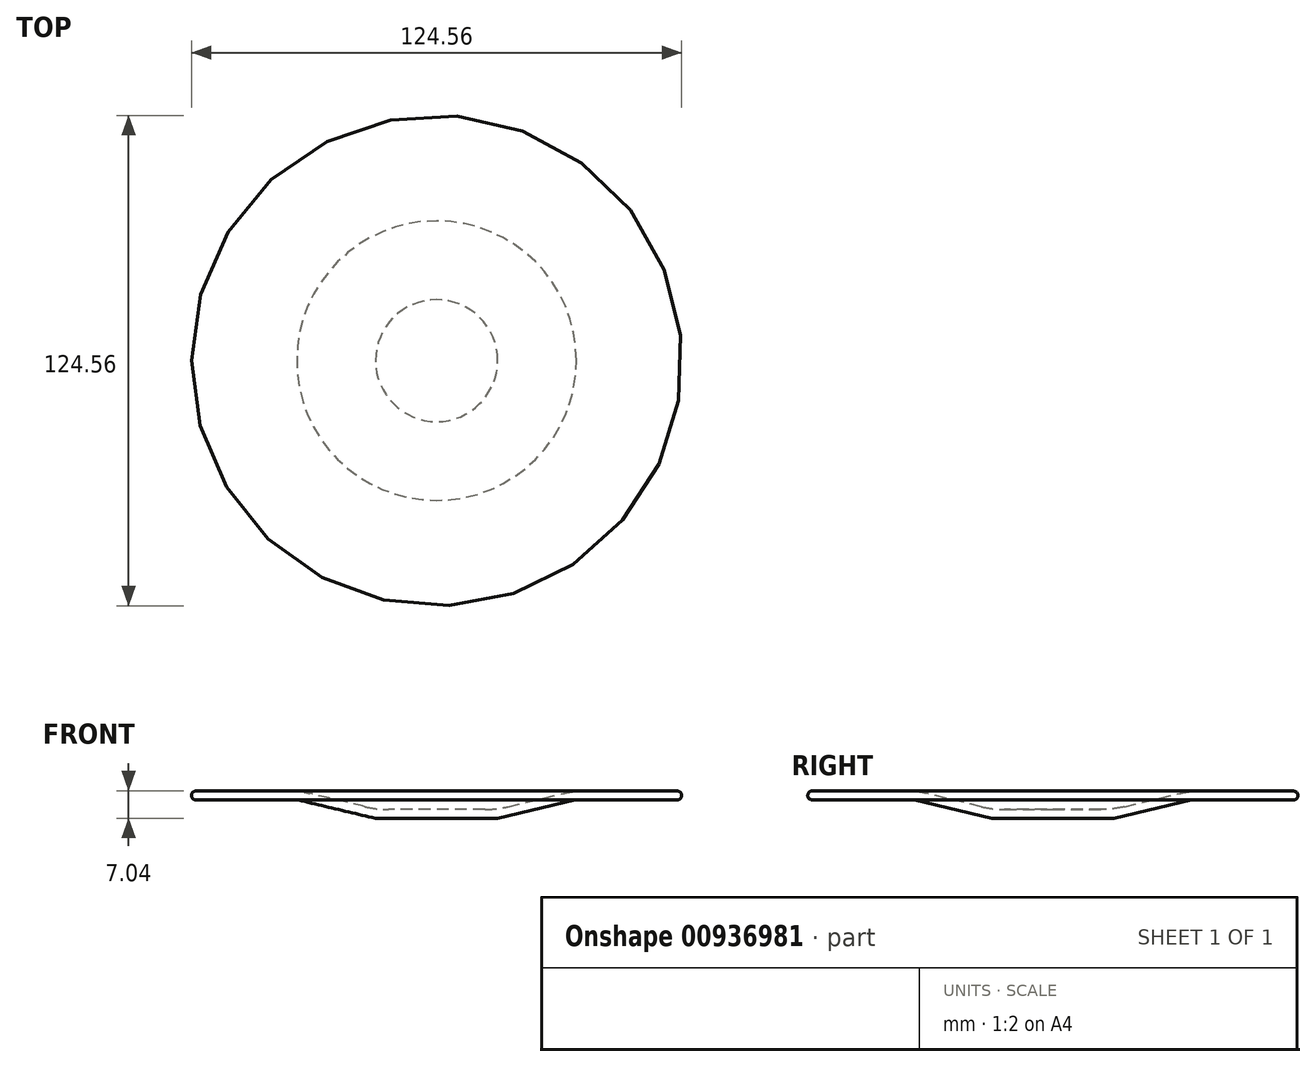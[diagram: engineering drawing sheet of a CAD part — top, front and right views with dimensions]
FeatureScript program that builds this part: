
annotation { "Feature Type Name" : "Feature", "Feature Type Description" : "" }
export const myFeature = defineFeature(function(context is Context, id is Id, definition is map)
    precondition{}
    {
        {
            var Q0;
            Q0=qCreatedBy(makeId("Front.planeOp"),FACE);
            var sketch = newSketch(context, id + "F0", { "sketchPlane" : qUnion([Q0])});
            skLineSegment(sketch, "E0", {"start": v(15.24, 0) * mm, "end": v(0, 0) * mm});
            skLineSegment(sketch, "E1", {"start": v(15.24, 0) * mm, "end": v(35.24, 4.76) * mm});
            skLineSegment(sketch, "E2", {"start": v(35.24, 4.76) * mm, "end": v(61.14, 4.68) * mm});
            skLineSegment(sketch, "E3", {"start": v(0, 0) * mm, "end": v(0, -2.29) * mm});
            skLineSegment(sketch, "E4.0", {"start": v(15.5, -2.29) * mm, "end": v(0, -2.29) * mm});
            skLineSegment(sketch, "E4.1", {"start": v(15.5, -2.29) * mm, "end": v(35.5, 2.47) * mm});
            skLineSegment(sketch, "E4.2", {"start": v(35.5, 2.47) * mm, "end": v(61.14, 2.39) * mm});
            skArc(sketch, "E5", {"start": v(61.14, 2.39) * mm, "mid": v(62.28, 3.53) * mm, "end": v(61.14, 4.68) * mm});
            skSolve(sketch);
        }
        {
            var Q0;
            Q0=qCreatedBy(makeId("Front.planeOp"),FACE);
            var sketch = newSketch(context, id + "F1", { "sketchPlane" : qUnion([Q0])});
            skLineSegment(sketch, "E6", {"start": v(0, -16.07) * mm, "end": v(0, 24.38) * mm, "construction": true});
            skSolve(sketch);
        }
        {
            var Q0;
            Q0=makeQuery(id+"F0.imprint","IMPRINT",FACE,{"disambiguationData":[TD([[makeQuery(id+"F0.imprint","IMPRINT",EDGE,{"derivedFrom":sQuery(id+"F0.wireOp",EDGE,"E0")}),1.0]])]});
            var Q1;
            Q1=sQuery(id+"F1.wireOp",EDGE,"E6");
            revolve(context, id + "F2", {"surfaceOperationType" : NewSurfaceOperationType.NEW, "entities" : qUnion([Q0]), "axis" : qUnion([Q1]), "revolveType" : RevolveType.FULL});
        }
        {
            var Q0;
            Q0=makeQuery(id+"F2.opRevolve","SWEPT_EDGE",EDGE,{"disambiguationData":[OSD([sQuery(id+"F0.wireOp",EDGE,"E1"),sQuery(id+"F0.wireOp",EDGE,"E2")])]});
            var Q1;
            Q1=makeQuery(id+"F2.opRevolve","SWEPT_EDGE",EDGE,{"disambiguationData":[OSD([sQuery(id+"F0.wireOp",EDGE,"E0"),sQuery(id+"F0.wireOp",EDGE,"E1")])]});
            fillet(context, id + "F3", {"entities" : qUnion([Q0, Q1]), "radius" : 25.4 * mm, "tangentPropagation" : true, "allowEdgeOverflow" : false});
        }
    });
